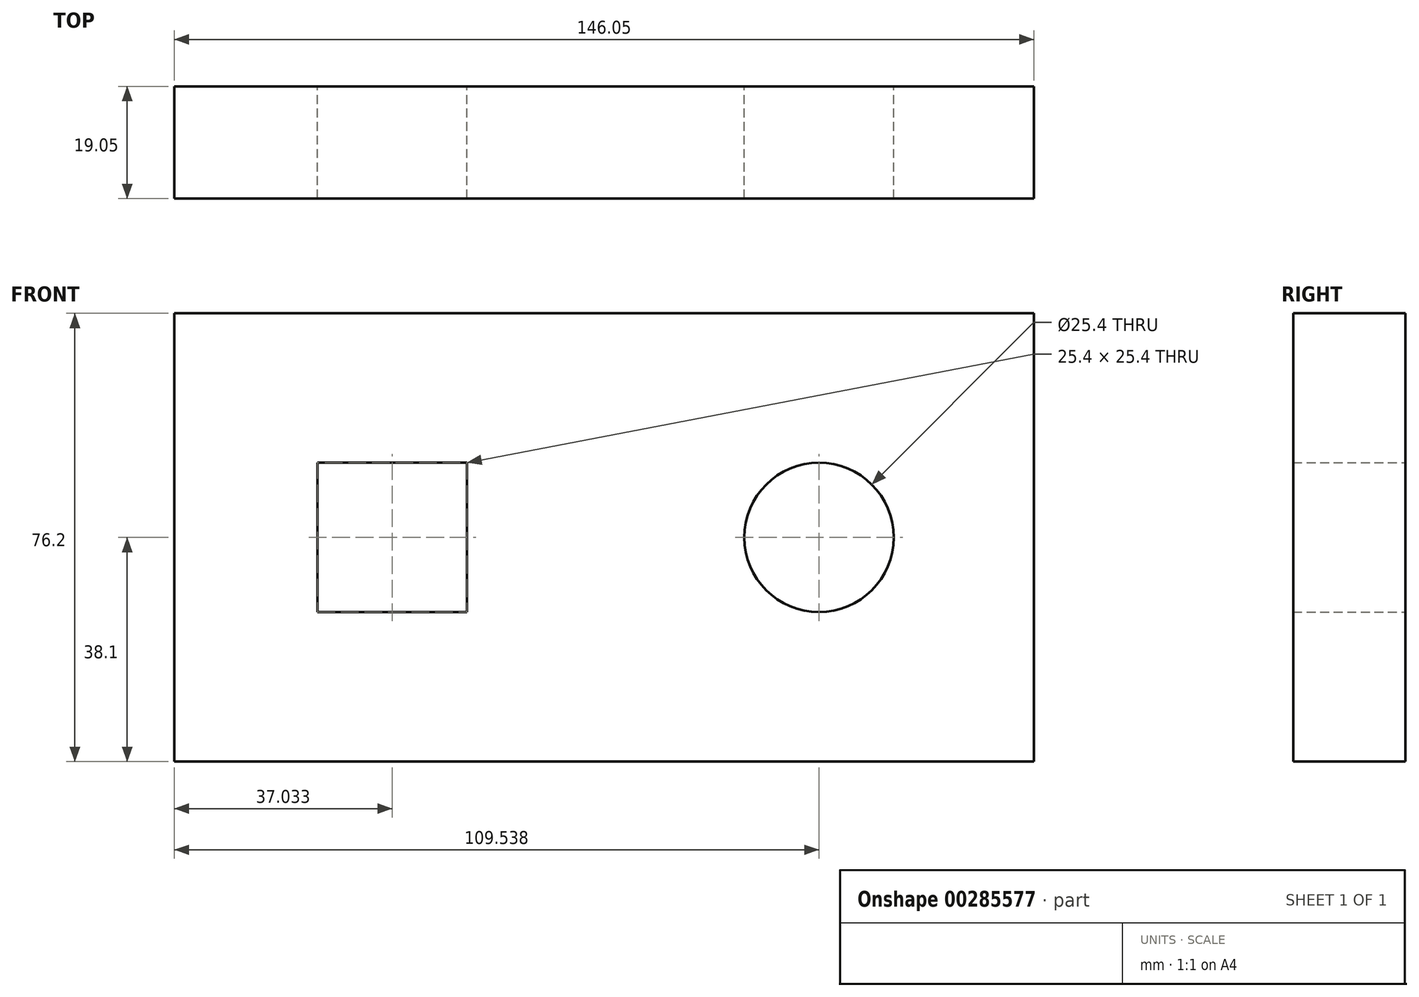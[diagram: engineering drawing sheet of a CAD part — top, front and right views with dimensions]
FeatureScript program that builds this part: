
annotation { "Feature Type Name" : "Feature", "Feature Type Description" : "" }
export const myFeature = defineFeature(function(context is Context, id is Id, definition is map)
    precondition{}
    {
        {
            var Q0;
            Q0=qCreatedBy(makeId("Front.planeOp"),FACE);
            var sketch = newSketch(context, id + "F0", { "sketchPlane" : qUnion([Q0])});
            skLineSegment(sketch, "E0.bottom", {"start": v(0, 0) * mm, "end": v(-146.05, 0) * mm});
            skLineSegment(sketch, "E0.top", {"start": v(0, 76.2) * mm, "end": v(-146.05, 76.2) * mm});
            skLineSegment(sketch, "E0.left", {"start": v(0, 0) * mm, "end": v(0, 76.2) * mm});
            skLineSegment(sketch, "E0.right", {"start": v(-146.05, 0) * mm, "end": v(-146.05, 76.2) * mm});
            skCircle(sketch, "E1", {"center": v(-36.51, 38.1) * mm, "radius": 12.7 * mm});
            skLineSegment(sketch, "E2.bottom", {"start": v(-121.72, 50.8) * mm, "end": v(-96.32, 50.8) * mm});
            skLineSegment(sketch, "E2.top", {"start": v(-121.72, 25.4) * mm, "end": v(-96.32, 25.4) * mm});
            skLineSegment(sketch, "E2.left", {"start": v(-121.72, 50.8) * mm, "end": v(-121.72, 25.4) * mm});
            skLineSegment(sketch, "E2.right", {"start": v(-96.32, 50.8) * mm, "end": v(-96.32, 25.4) * mm});
            skSolve(sketch);
        }
        {
            var Q0;
            Q0=makeQuery(id+"F0.imprint","IMPRINT",FACE,{"disambiguationData":[TD([[makeQuery(id+"F0.imprint","IMPRINT",EDGE,{"derivedFrom":sQuery(id+"F0.wireOp",EDGE,"E0.bottom")}),-1.0]])]});
            extrude(context, id + "F1", {"entities" : qUnion([Q0]), "depth" : 19.05 * mm});
        }
    });
